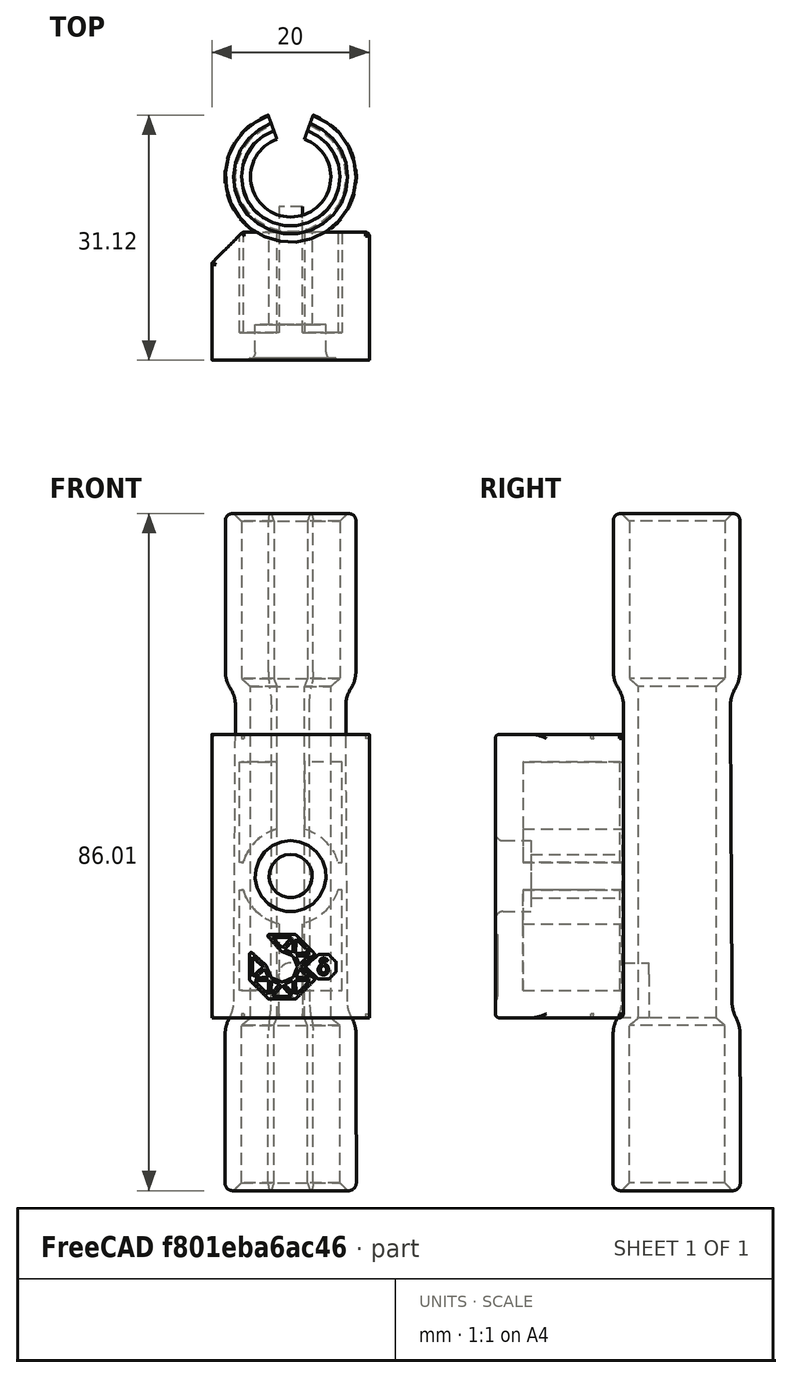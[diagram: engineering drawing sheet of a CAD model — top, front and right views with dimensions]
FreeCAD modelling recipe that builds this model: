
FCSTD DOCUMENT  (FreeCAD 0.18R16146 (Git))
Label: VerticalSlider
License: All rights reserved
LicenseURL: http://en.wikipedia.org/wiki/All_rights_reserved
objects: PartDesign::Chamfer×2, Sketcher::SketchObject×1, PartDesign::Revolution×1, Mesh::Feature×1, PartDesign::Body×1, Part::Feature×1, Part::Box×1, Part::MultiCommon×1, Spreadsheet::Sheet×1
note: 9 computed .brp shape members not serialized (recipe doc carries the construction recipe); baked Part::Feature solids carry a one-line shape summary decoded from their .brp

FEATURE [Sketcher::SketchObject] Sketch
  MapMode = 5
  Placement = pos=(0,0,0) rot=(1,0,0;1.5708rad)
  Support = -> [XZ_Plane]
  sketch-geometry (19):
    g0: BSplineCurve PolesCount=2 KnotsCount=2 Degree=1 IsPeriodic=0
    g1: BSplineCurve PolesCount=2 KnotsCount=2 Degree=1 IsPeriodic=0
    g2: BSplineCurve PolesCount=2 KnotsCount=2 Degree=1 IsPeriodic=0
    g3: BSplineCurve PolesCount=2 KnotsCount=2 Degree=1 IsPeriodic=0
    g4: BSplineCurve PolesCount=2 KnotsCount=2 Degree=1 IsPeriodic=0
    g5: BSplineCurve PolesCount=2 KnotsCount=2 Degree=1 IsPeriodic=0
    g6: BSplineCurve PolesCount=2 KnotsCount=2 Degree=1 IsPeriodic=0
    g7: LineSegment StartX=-5.1 StartY=64.0896 StartZ=0 EndX=-5.1 EndY=64.0896 EndZ=0
    g8: BSplineCurve PolesCount=2 KnotsCount=2 Degree=1 IsPeriodic=0
    g9: BSplineCurve PolesCount=2 KnotsCount=2 Degree=1 IsPeriodic=0
    g10: BSplineCurve PolesCount=2 KnotsCount=2 Degree=1 IsPeriodic=0
    g11: BSplineCurve PolesCount=2 KnotsCount=2 Degree=1 IsPeriodic=0
    g12: BSplineCurve PolesCount=2 KnotsCount=2 Degree=1 IsPeriodic=0
    g13: ArcOfCircle CenterX=-4.47437 CenterY=65.9516 CenterZ=0 NormalX=0 NormalY=0 NormalZ=1 AngleXU=0 Radius=3.80826 StartAngle=3.14193 EndAngle=3.71015
    g14: ArcOfCircle CenterX=-11.1637 CenterY=61.6203 CenterZ=0 NormalX=0 NormalY=0 NormalZ=1 AngleXU=0 Radius=4.16073 StartAngle=6.27741 EndAngle=6.85175
    g15: ArcOfCircle CenterX=-3.93931 CenterY=19.8763 CenterZ=0 NormalX=0 NormalY=0 NormalZ=1 AngleXU=0 Radius=4.37905 StartAngle=2.6662 EndAngle=3.14025
    g16: ArcOfCircle CenterX=-11.4659 CenterY=24.1002 CenterZ=0 NormalX=0 NormalY=0 NormalZ=1 AngleXU=0 Radius=4.24619 StartAngle=5.8078 EndAngle=6.27741
    g17: ArcOfCircle CenterX=-7.41556 CenterY=85.1716 CenterZ=0 NormalX=0 NormalY=0 NormalZ=1 AngleXU=0 Radius=0.873555 StartAngle=1.60839 EndAngle=3.14193
    g18: ArcOfCircle CenterX=-7.36046 CenterY=1.02255 CenterZ=0 NormalX=0 NormalY=0 NormalZ=1 AngleXU=0 Radius=0.983162 StartAngle=3.14025 EndAngle=4.71465
  constraints (28):
    c: Coincident(g0,g4)
    c: Coincident(g4,g5)
    c: Coincident(g5,g6)
    c: Coincident(g6,g7)
    c: Horizontal(g7)
    c: Coincident(g10,g11)
    c: Coincident(g11,g12)
    c: Coincident(g12,g6)
    c: DistanceX(g0,g-1) = 6.25
    c: DistanceX(g4,g-1) = 6.25
    c: DistanceX(g5,g-1) = 5.1
    c: DistanceX(g-2,g11) = -6.25
    c: DistanceX(g-2,g10) = -6.25
    c: DistanceY(g0,g4) = 21
    c: DistanceY(g11,g10) = 21
    c: DistanceY(g6,g11) = 1
    c: Tangent(g9,g13) = 1.5708
    c: Tangent(g8,g13) = 1.5708
    c: Tangent(g8,g14) = -1.5708
    c: Tangent(g3,g14) = -1.5708
    c: Tangent(g1,g15) = 1.5708
    c: Tangent(g2,g15) = 1.5708
    c: Tangent(g2,g16) = -1.5708
    c: Tangent(g3,g16) = -1.5708
    c: Tangent(g9,g17) = 1.5708
    c: Tangent(g10,g17) = 1.5708
    c: Tangent(g1,g18) = 1.5708
    c: Tangent(g0,g18) = 1.5708
FEATURE [PartDesign::Revolution] Revolution
  Angle = 320
  Axis = (-3e-16,3e-16,1)
  Base = (0,0,0)
  Midplane = true
  Placement = pos=(0,0,0) rot=(1,0,0;1.5708rad)
  Profile = -> Sketch
  ReferenceAxis = -> Z_Axis
FEATURE [Mesh::Feature] K8800_VS_Generic  label="K8800-VS-Generic"
  Placement = pos=(0,0,60) rot=(1,0,0;3.14159rad)
FEATURE [PartDesign::Chamfer] Chamfer
  Base = -> Revolution [Edge41]
  BaseFeature = -> Revolution
  Placement = pos=(0,0,0) rot=(1,0,0;1.5708rad)
  Size = 1
FEATURE [PartDesign::Chamfer] Chamfer001
  Base = -> Chamfer [Edge53]
  BaseFeature = -> Chamfer
  Placement = pos=(0,0,0) rot=(1,0,0;1.5708rad)
  Size = 1
FEATURE [PartDesign::Body] Body  label="Bearingholder"
  Group = -> [Sketch,Revolution,Chamfer,Chamfer001]
  Origin = -> Origin
  Placement = pos=(0,0,0) rot=(0,0,1;1.5708rad)
  Tip = -> Chamfer001
FEATURE [Part::Feature] K8800_VS
  shape: bbox 24.93 x 72.01 x 46.6 mm, 535 faces (baked)
FEATURE [Part::Box] Box  label="Würfel"
  AttacherType = Attacher::AttachEngine3D
  Height = 36
  Length = 20
  Placement = pos=(-23.3,-10,-18) rot=(0,0,1;0rad)
  Width = 20
FEATURE [Part::MultiCommon] Common  label="Beltholdblock"
  Placement = pos=(0,0,40) rot=(0,0,1;1.5708rad)
  Shapes = -> [K8800_VS,Box]
FEATURE [Spreadsheet::Sheet] Spreadsheet
  cells = A1(LW)==0.33mm; B1=line width; A2(riBearing)==5mm; B2=bearing: inner radius; A3(roBearing)==6.5mm; B3=bearing: outer radius; A4(lenBearing)==20mm; B4=bearing: length; A5==4 * LW; B5=bearing holder: wall thickness
